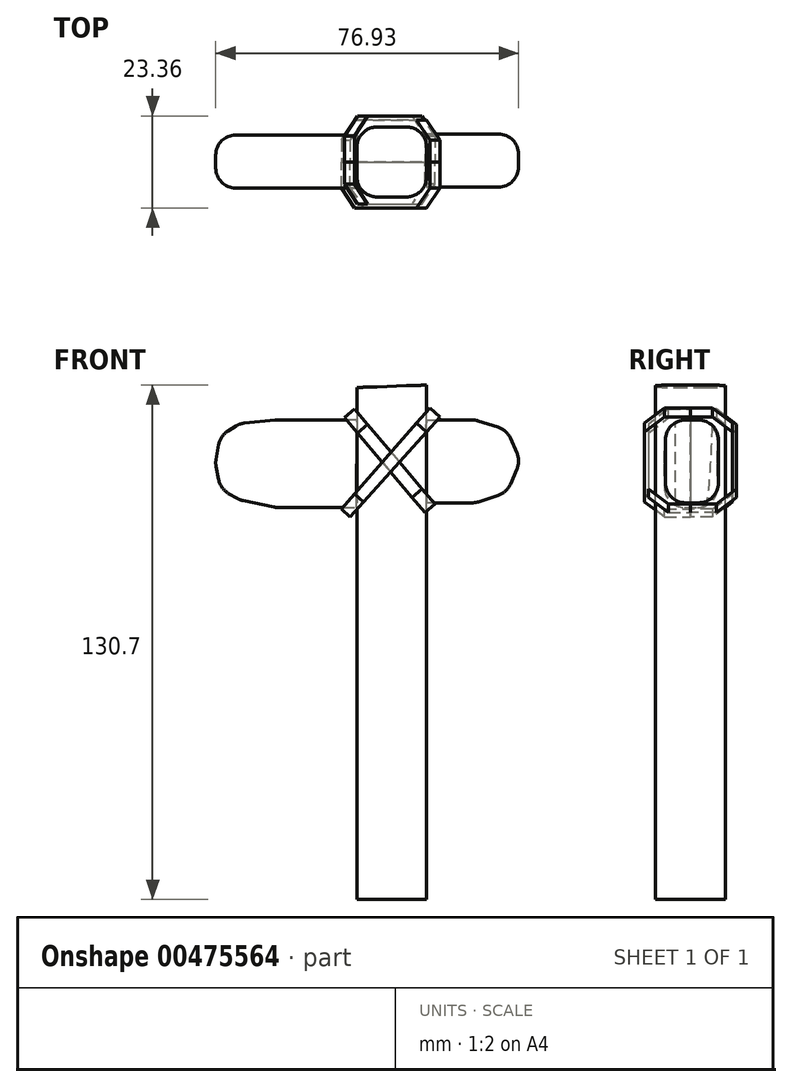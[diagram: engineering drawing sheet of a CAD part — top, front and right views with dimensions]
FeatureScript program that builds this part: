
annotation { "Feature Type Name" : "Feature", "Feature Type Description" : "" }
export const myFeature = defineFeature(function(context is Context, id is Id, definition is map)
    precondition{}
    {
        {
            var Q0;
            Q0=qCreatedBy(makeId("Front.planeOp"),FACE);
            var sketch = newSketch(context, id + "F0", { "sketchPlane" : qUnion([Q0])});
            skLineSegment(sketch, "E0", {"start": v(-9.77, 54.36) * mm, "end": v(-30.3, 54.36) * mm});
            skLineSegment(sketch, "E1", {"start": v(-30.3, 54.36) * mm, "end": v(-39.44, 53.45) * mm});
            skLineSegment(sketch, "E2", {"start": v(-39.44, 53.45) * mm, "end": v(-44.47, 50.36) * mm});
            skLineSegment(sketch, "E3", {"start": v(-44.47, 36.89) * mm, "end": v(-39.44, 34) * mm});
            skLineSegment(sketch, "E4", {"start": v(-39.44, 34) * mm, "end": v(-30.3, 32.1) * mm});
            skLineSegment(sketch, "E5", {"start": v(-30.3, 32.1) * mm, "end": v(-9.83, 32.1) * mm});
            skLineSegment(sketch, "E6", {"start": v(-9.77, 54.36) * mm, "end": v(-9.83, 32.1) * mm});
            skLineSegment(sketch, "E7", {"start": v(-44.47, 36.89) * mm, "end": v(-45.73, 43.42) * mm});
            skLineSegment(sketch, "E8", {"start": v(-45.73, 43.42) * mm, "end": v(-44.47, 50.36) * mm});
            skSolve(sketch);
        }
        {
            var Q0;
            Q0=qCreatedBy(makeId("Front.planeOp"),FACE);
            var sketch = newSketch(context, id + "F1", { "sketchPlane" : qUnion([Q0])});
            skLineSegment(sketch, "E9", {"start": v(7.63, 54.36) * mm, "end": v(20.28, 54.36) * mm});
            skLineSegment(sketch, "E10", {"start": v(20.28, 54.36) * mm, "end": v(28.27, 51.83) * mm});
            skLineSegment(sketch, "E11", {"start": v(28.27, 35.93) * mm, "end": v(20.28, 33.29) * mm});
            skLineSegment(sketch, "E12", {"start": v(20.28, 33.29) * mm, "end": v(7.94, 33.29) * mm});
            skLineSegment(sketch, "E13", {"start": v(28.27, 51.83) * mm, "end": v(31.76, 43.93) * mm});
            skLineSegment(sketch, "E14", {"start": v(28.27, 35.93) * mm, "end": v(31.76, 43.93) * mm});
            skLineSegment(sketch, "E15", {"start": v(7.63, 54.36) * mm, "end": v(7.94, 33.29) * mm});
            skSolve(sketch);
        }
        {
            var Q0;
            Q0=qCreatedBy(makeId("Front.planeOp"),FACE);
            var sketch = newSketch(context, id + "F2", { "sketchPlane" : qUnion([Q0])});
            skLineSegment(sketch, "E16", {"start": v(-9.77, 62.6) * mm, "end": v(-9.77, -67.49) * mm});
            skLineSegment(sketch, "E17", {"start": v(-9.77, -67.49) * mm, "end": v(7.94, -67.49) * mm});
            skLineSegment(sketch, "E18", {"start": v(7.94, -67.49) * mm, "end": v(7.94, 63.21) * mm});
            skLineSegment(sketch, "E19", {"start": v(7.94, 63.21) * mm, "end": v(-9.77, 62.6) * mm});
            skSolve(sketch);
        }
        {
            var Q0;
            Q0=makeQuery(id+"F2.imprint","IMPRINT",FACE,{"disambiguationData":[TD([[makeQuery(id+"F2.imprint","IMPRINT",EDGE,{"derivedFrom":sQuery(id+"F2.wireOp",EDGE,"E16")}),1.0]])]});
            extrude(context, id + "F3", {"entities" : qUnion([Q0]), "depth" : 8.9 * mm});
        }
        {
            var Q0;
            Q0=makeQuery(id+"F3.opExtrude","CAP_FACE",FACE,{"disambiguationData":[OSD([sQuery(id+"F2.wireOp",EDGE,"E16"),sQuery(id+"F2.wireOp",EDGE,"E17"),sQuery(id+"F2.wireOp",EDGE,"E18"),sQuery(id+"F2.wireOp",EDGE,"E19")])],"isStart":true});
            extrude(context, id + "F4", {"entities" : qUnion([Q0]), "operationType" : NewBodyOperationType.ADD, "depth" : 8.9 * mm});
        }
        {
            var Q0;
            Q0=makeQuery(id+"F3.opExtrude","CAP_EDGE",EDGE,{"disambiguationData":[OSD([sQuery(id+"F2.wireOp",EDGE,"E18")])],"isStart":false});
            var Q1;
            Q1=makeQuery(id+"F4.opExtrude","CAP_EDGE",EDGE,{"disambiguationData":[OSD([sQuery(id+"F2.wireOp",EDGE,"E18")])],"isStart":false});
            var Q2;
            Q2=makeQuery(id+"F3.opExtrude","CAP_EDGE",EDGE,{"disambiguationData":[OSD([sQuery(id+"F2.wireOp",EDGE,"E16")])],"isStart":false});
            var Q3;
            Q3=makeQuery(id+"F4.opExtrude","CAP_EDGE",EDGE,{"disambiguationData":[OSD([sQuery(id+"F2.wireOp",EDGE,"E16")])],"isStart":false});
            fillet(context, id + "F5", {"entities" : qUnion([Q0, Q1, Q2, Q3]), "radius" : 5.08 * mm, "tangentPropagation" : true, "allowEdgeOverflow" : false});
        }
        {
            var Q0;
            Q0=makeQuery(id+"F0.imprint","IMPRINT",FACE,{"disambiguationData":[TD([[makeQuery(id+"F0.imprint","IMPRINT",EDGE,{"derivedFrom":sQuery(id+"F0.wireOp",EDGE,"E0")}),1.0]])]});
            extrude(context, id + "F6", {"entities" : qUnion([Q0]), "depth" : 6.6 * mm});
        }
        {
            var Q0;
            Q0=makeQuery(id+"F6.opExtrude","CAP_FACE",FACE,{"disambiguationData":[OSD([sQuery(id+"F0.wireOp",EDGE,"E0"),sQuery(id+"F0.wireOp",EDGE,"E1"),sQuery(id+"F0.wireOp",EDGE,"E2"),sQuery(id+"F0.wireOp",EDGE,"q3bksTcm-MVQw-fvwo-Y89u-pe7UXle7tT1u"),sQuery(id+"F0.wireOp",EDGE,"E3"),sQuery(id+"F0.wireOp",EDGE,"E4"),sQuery(id+"F0.wireOp",EDGE,"E5"),sQuery(id+"F0.wireOp",EDGE,"E6")])],"isStart":true});
            extrude(context, id + "F7", {"entities" : qUnion([Q0]), "operationType" : NewBodyOperationType.ADD, "depth" : 6.86 * mm});
        }
        {
            var Q0;
            {var subQ0=sQuery(id+"F0.wireOp",EDGE,"E1");var subQ1=sQuery(id+"F0.wireOp",EDGE,"E0");Q0=makeQuery(id+"F7.boolean.opBoolean","MERGE",EDGE,{"derivedFrom":[makeQuery(id+"F6.opExtrude","SWEPT_EDGE",EDGE,{"disambiguationData":[OSD([subQ1,subQ0])]}),makeQuery(id+"F7.opExtrude","SWEPT_EDGE",EDGE,{"disambiguationData":[OSD([subQ1,subQ0])]})]});}
            var Q1;
            {var subQ0=sQuery(id+"F0.wireOp",EDGE,"E2");var subQ1=sQuery(id+"F0.wireOp",EDGE,"E1");Q1=makeQuery(id+"F7.boolean.opBoolean","MERGE",EDGE,{"derivedFrom":[makeQuery(id+"F6.opExtrude","SWEPT_EDGE",EDGE,{"disambiguationData":[OSD([subQ1,subQ0])]}),makeQuery(id+"F7.opExtrude","SWEPT_EDGE",EDGE,{"disambiguationData":[OSD([subQ1,subQ0])]})]});}
            var Q2;
            {var subQ0=sQuery(id+"F0.wireOp",EDGE,"q3bksTcm-MVQw-fvwo-Y89u-pe7UXle7tT1u");var subQ1=sQuery(id+"F0.wireOp",EDGE,"E2");Q2=makeQuery(id+"F7.boolean.opBoolean","MERGE",EDGE,{"derivedFrom":[makeQuery(id+"F6.opExtrude","SWEPT_EDGE",EDGE,{"disambiguationData":[OSD([subQ1,subQ0])]}),makeQuery(id+"F7.opExtrude","SWEPT_EDGE",EDGE,{"disambiguationData":[OSD([subQ1,subQ0])]})]});}
            var Q3;
            {var subQ0=sQuery(id+"F0.wireOp",EDGE,"E3");var subQ1=sQuery(id+"F0.wireOp",EDGE,"q3bksTcm-MVQw-fvwo-Y89u-pe7UXle7tT1u");Q3=makeQuery(id+"F7.boolean.opBoolean","MERGE",EDGE,{"derivedFrom":[makeQuery(id+"F6.opExtrude","SWEPT_EDGE",EDGE,{"disambiguationData":[OSD([subQ1,subQ0])]}),makeQuery(id+"F7.opExtrude","SWEPT_EDGE",EDGE,{"disambiguationData":[OSD([subQ1,subQ0])]})]});}
            var Q4;
            {var subQ0=sQuery(id+"F0.wireOp",EDGE,"E4");var subQ1=sQuery(id+"F0.wireOp",EDGE,"E3");Q4=makeQuery(id+"F7.boolean.opBoolean","MERGE",EDGE,{"derivedFrom":[makeQuery(id+"F6.opExtrude","SWEPT_EDGE",EDGE,{"disambiguationData":[OSD([subQ1,subQ0])]}),makeQuery(id+"F7.opExtrude","SWEPT_EDGE",EDGE,{"disambiguationData":[OSD([subQ1,subQ0])]})]});}
            var Q5;
            {var subQ0=sQuery(id+"F0.wireOp",EDGE,"E5");var subQ1=sQuery(id+"F0.wireOp",EDGE,"E4");Q5=makeQuery(id+"F7.boolean.opBoolean","MERGE",EDGE,{"derivedFrom":[makeQuery(id+"F6.opExtrude","SWEPT_EDGE",EDGE,{"disambiguationData":[OSD([subQ1,subQ0])]}),makeQuery(id+"F7.opExtrude","SWEPT_EDGE",EDGE,{"disambiguationData":[OSD([subQ1,subQ0])]})]});}
            fillet(context, id + "F8", {"entities" : qUnion([Q0, Q1, Q2, Q3, Q4, Q5]), "radius" : 5.08 * mm, "tangentPropagation" : true, "allowEdgeOverflow" : false});
        }
        {
            var Q0;
            Q0=makeQuery(id+"F1.imprint","IMPRINT",FACE,{"disambiguationData":[TD([[makeQuery(id+"F1.imprint","IMPRINT",EDGE,{"derivedFrom":sQuery(id+"F1.wireOp",EDGE,"E9")}),-1.0]])]});
            extrude(context, id + "F9", {"entities" : qUnion([Q0]), "operationType" : NewBodyOperationType.ADD, "oppositeDirection" : true, "depth" : 7.11 * mm});
        }
        {
            var Q0;
            Q0=makeQuery(id+"F9.opExtrude","CAP_FACE",FACE,{"disambiguationData":[OSD([sQuery(id+"F1.wireOp",EDGE,"E9"),sQuery(id+"F1.wireOp",EDGE,"E10"),sQuery(id+"F1.wireOp",EDGE,"E11"),sQuery(id+"F1.wireOp",EDGE,"E12"),sQuery(id+"F1.wireOp",EDGE,"E13"),sQuery(id+"F1.wireOp",EDGE,"E14"),sQuery(id+"F1.wireOp",EDGE,"E15")])],"isStart":true});
            extrude(context, id + "F10", {"entities" : qUnion([Q0]), "operationType" : NewBodyOperationType.ADD, "depth" : 6.35 * mm});
        }
        {
            var Q0;
            {var subQ0=sQuery(id+"F1.wireOp",EDGE,"E10");var subQ1=sQuery(id+"F1.wireOp",EDGE,"E9");Q0=makeQuery(id+"F10.boolean.opBoolean","MERGE",EDGE,{"derivedFrom":[makeQuery(id+"F9.opExtrude","SWEPT_EDGE",EDGE,{"disambiguationData":[OSD([subQ1,subQ0])]}),makeQuery(id+"F10.opExtrude","SWEPT_EDGE",EDGE,{"disambiguationData":[OSD([subQ1,subQ0])]})]});}
            var Q1;
            {var subQ0=sQuery(id+"F1.wireOp",EDGE,"E13");var subQ1=sQuery(id+"F1.wireOp",EDGE,"E10");Q1=makeQuery(id+"F10.boolean.opBoolean","MERGE",EDGE,{"derivedFrom":[makeQuery(id+"F9.opExtrude","SWEPT_EDGE",EDGE,{"disambiguationData":[OSD([subQ1,subQ0])]}),makeQuery(id+"F10.opExtrude","SWEPT_EDGE",EDGE,{"disambiguationData":[OSD([subQ1,subQ0])]})]});}
            var Q2;
            {var subQ0=sQuery(id+"F1.wireOp",EDGE,"E14");var subQ1=sQuery(id+"F1.wireOp",EDGE,"E13");Q2=makeQuery(id+"F10.boolean.opBoolean","MERGE",EDGE,{"derivedFrom":[makeQuery(id+"F9.opExtrude","SWEPT_EDGE",EDGE,{"disambiguationData":[OSD([subQ1,subQ0])]}),makeQuery(id+"F10.opExtrude","SWEPT_EDGE",EDGE,{"disambiguationData":[OSD([subQ1,subQ0])]})]});}
            var Q3;
            {var subQ0=sQuery(id+"F1.wireOp",EDGE,"E14");var subQ1=sQuery(id+"F1.wireOp",EDGE,"E11");Q3=makeQuery(id+"F10.boolean.opBoolean","MERGE",EDGE,{"derivedFrom":[makeQuery(id+"F9.opExtrude","SWEPT_EDGE",EDGE,{"disambiguationData":[OSD([subQ1,subQ0])]}),makeQuery(id+"F10.opExtrude","SWEPT_EDGE",EDGE,{"disambiguationData":[OSD([subQ1,subQ0])]})]});}
            var Q4;
            {var subQ0=sQuery(id+"F1.wireOp",EDGE,"E12");var subQ1=sQuery(id+"F1.wireOp",EDGE,"E11");Q4=makeQuery(id+"F10.boolean.opBoolean","MERGE",EDGE,{"derivedFrom":[makeQuery(id+"F9.opExtrude","SWEPT_EDGE",EDGE,{"disambiguationData":[OSD([subQ1,subQ0])]}),makeQuery(id+"F10.opExtrude","SWEPT_EDGE",EDGE,{"disambiguationData":[OSD([subQ1,subQ0])]})]});}
            fillet(context, id + "F11", {"entities" : qUnion([Q0, Q1, Q2, Q3, Q4]), "radius" : 5.08 * mm, "tangentPropagation" : true, "allowEdgeOverflow" : false});
        }
        {
            var Q0;
            {var subQ0=sQuery(id+"F0.wireOp",EDGE,"E8");var subQ1=sQuery(id+"F0.wireOp",EDGE,"E7");Q0=makeQuery(id+"F7.boolean.opBoolean","MERGE",EDGE,{"derivedFrom":[makeQuery(id+"F6.opExtrude","SWEPT_EDGE",EDGE,{"disambiguationData":[OSD([subQ1,subQ0])]}),makeQuery(id+"F7.opExtrude","SWEPT_EDGE",EDGE,{"disambiguationData":[OSD([subQ1,subQ0])]})]});}
            fillet(context, id + "F12", {"entities" : qUnion([Q0]), "radius" : 5.08 * mm, "tangentPropagation" : true, "allowEdgeOverflow" : false});
        }
        {
            var Q0;
            Q0=qCreatedBy(makeId("Front.planeOp"),FACE);
            var sketch = newSketch(context, id + "F13", { "sketchPlane" : qUnion([Q0])});
            skLineSegment(sketch, "E20", {"start": v(-10.38, 57.1) * mm, "end": v(10.08, 32.98) * mm});
            skLineSegment(sketch, "E21", {"start": v(-10.38, 57.1) * mm, "end": v(-12.96, 54.92) * mm});
            skLineSegment(sketch, "E22", {"start": v(-12.96, 54.92) * mm, "end": v(7.53, 30.78) * mm});
            skLineSegment(sketch, "E23", {"start": v(7.53, 30.78) * mm, "end": v(10.08, 32.98) * mm});
            skSolve(sketch);
        }
        {
            var Q0;
            Q0 = qSketchRegion(id + "F13", true);
            extrude(context, id + "F14", {"entities" : qUnion([Q0]), "depth" : 10.67 * mm});
        }
        {
            var Q0;
            Q0=qCreatedBy(makeId("Front.planeOp"),FACE);
            var sketch = newSketch(context, id + "F15", { "sketchPlane" : qUnion([Q0])});
            skLineSegment(sketch, "E24", {"start": v(8.73, 57.44) * mm, "end": v(11.36, 55.07) * mm});
            skLineSegment(sketch, "E25", {"start": v(11.36, 55.07) * mm, "end": v(-11.47, 29.72) * mm});
            skLineSegment(sketch, "E26", {"start": v(-11.47, 29.72) * mm, "end": v(-13.74, 31.76) * mm});
            skLineSegment(sketch, "E27", {"start": v(-13.74, 31.76) * mm, "end": v(8.73, 57.44) * mm});
            skSolve(sketch);
        }
        {
            var Q0;
            Q0 = qSketchRegion(id + "F15", true);
            extrude(context, id + "F16", {"entities" : qUnion([Q0]), "depth" : 11.68 * mm});
        }
        {
            var Q0;
            Q0 = qSketchRegion(id + "F15", true);
            extrude(context, id + "F17", {"entities" : qUnion([Q0]), "oppositeDirection" : true, "depth" : 10.67 * mm});
        }
        {
            var Q0;
            Q0 = qSketchRegion(id + "F13", true);
            extrude(context, id + "F18", {"entities" : qUnion([Q0]), "oppositeDirection" : true, "depth" : 11.68 * mm});
        }
        {
            var Q0;
            Q0=makeQuery(id+"F14.opExtrude","CAP_EDGE",EDGE,{"disambiguationData":[OSD([sQuery(id+"F13.wireOp",EDGE,"E21")])],"isStart":false});
            var Q1;
            Q1=makeQuery(id+"F16.opExtrude","CAP_EDGE",EDGE,{"disambiguationData":[OSD([sQuery(id+"F15.wireOp",EDGE,"E24")])],"isStart":false});
            var Q2;
            Q2=makeQuery(id+"F14.opExtrude","CAP_EDGE",EDGE,{"disambiguationData":[OSD([sQuery(id+"F13.wireOp",EDGE,"E23")])],"isStart":false});
            var Q3;
            Q3=makeQuery(id+"F16.opExtrude","CAP_EDGE",EDGE,{"disambiguationData":[OSD([sQuery(id+"F15.wireOp",EDGE,"E26")])],"isStart":false});
            var Q4;
            Q4=makeQuery(id+"F17.opExtrude","CAP_EDGE",EDGE,{"disambiguationData":[OSD([sQuery(id+"F15.wireOp",EDGE,"E24")])],"isStart":false});
            var Q5;
            Q5=makeQuery(id+"F18.opExtrude","CAP_EDGE",EDGE,{"disambiguationData":[OSD([sQuery(id+"F13.wireOp",EDGE,"E21")])],"isStart":false});
            var Q6;
            Q6=makeQuery(id+"F17.opExtrude","CAP_EDGE",EDGE,{"disambiguationData":[OSD([sQuery(id+"F15.wireOp",EDGE,"E26")])],"isStart":false});
            var Q7;
            Q7=makeQuery(id+"F18.opExtrude","CAP_EDGE",EDGE,{"disambiguationData":[OSD([sQuery(id+"F13.wireOp",EDGE,"E23")])],"isStart":false});
            chamfer(context, id + "F19", {"entities" : qUnion([Q0, Q1, Q2, Q3, Q4, Q5, Q6, Q7]), "width" : 5.08 * mm, "tangentPropagation" : true});
        }
        {
            var Q0;
            Q0=makeQuery(id+"F6.opExtrude","CAP_EDGE",EDGE,{"disambiguationData":[OSD([sQuery(id+"F0.wireOp",EDGE,"E0")])],"isStart":false});
            var Q1;
            Q1=makeQuery(id+"F7.opExtrude","CAP_EDGE",EDGE,{"disambiguationData":[OSD([sQuery(id+"F0.wireOp",EDGE,"E0")])],"isStart":false});
            var Q2;
            Q2=makeQuery(id+"F10.opExtrude","CAP_EDGE",EDGE,{"disambiguationData":[OSD([sQuery(id+"F1.wireOp",EDGE,"E9")])],"isStart":false});
            var Q3;
            Q3=makeQuery(id+"F9.opExtrude","CAP_EDGE",EDGE,{"disambiguationData":[OSD([sQuery(id+"F1.wireOp",EDGE,"E9")])],"isStart":false});
            fillet(context, id + "F20", {"entities" : qUnion([Q0, Q1, Q2, Q3]), "radius" : 5.08 * mm, "tangentPropagation" : true, "allowEdgeOverflow" : false});
        }
    });
